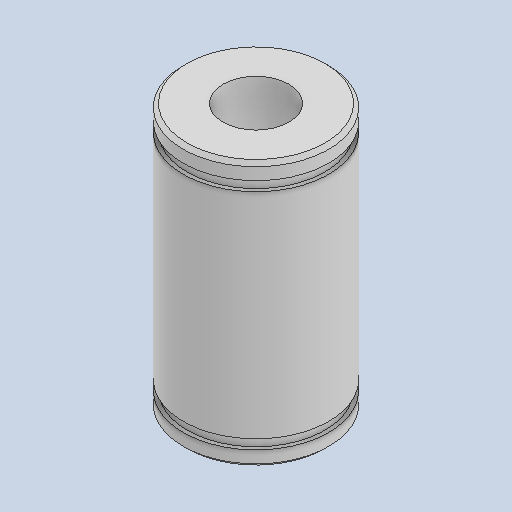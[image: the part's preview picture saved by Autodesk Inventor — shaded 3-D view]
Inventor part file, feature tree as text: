
AUTODESK INVENTOR PART (.ipt)
format: ipt  version: 2022 (Build 260153000, 153)  size: 113,664 bytes
history: native  units: in
note: dims shown in document units (in); Inventor stores cm internally (conversion verified against a paired STEP export)
features: chamfer x1
ambient origin geometry x8: Origin, YZ Plane, XZ Plane, XY Plane, X Axis, Y Axis, Z Axis, Center Point
bodies: Solid1 (feature_tree)
feature tree (1):
  chamfer  "Chamfer1"  [1 undecoded]
note: 1 required parameter value undecoded (feature->parameter linkage not recoverable at this tier; creation-order binding heuristic only, values carry confidence <= 0.55)
